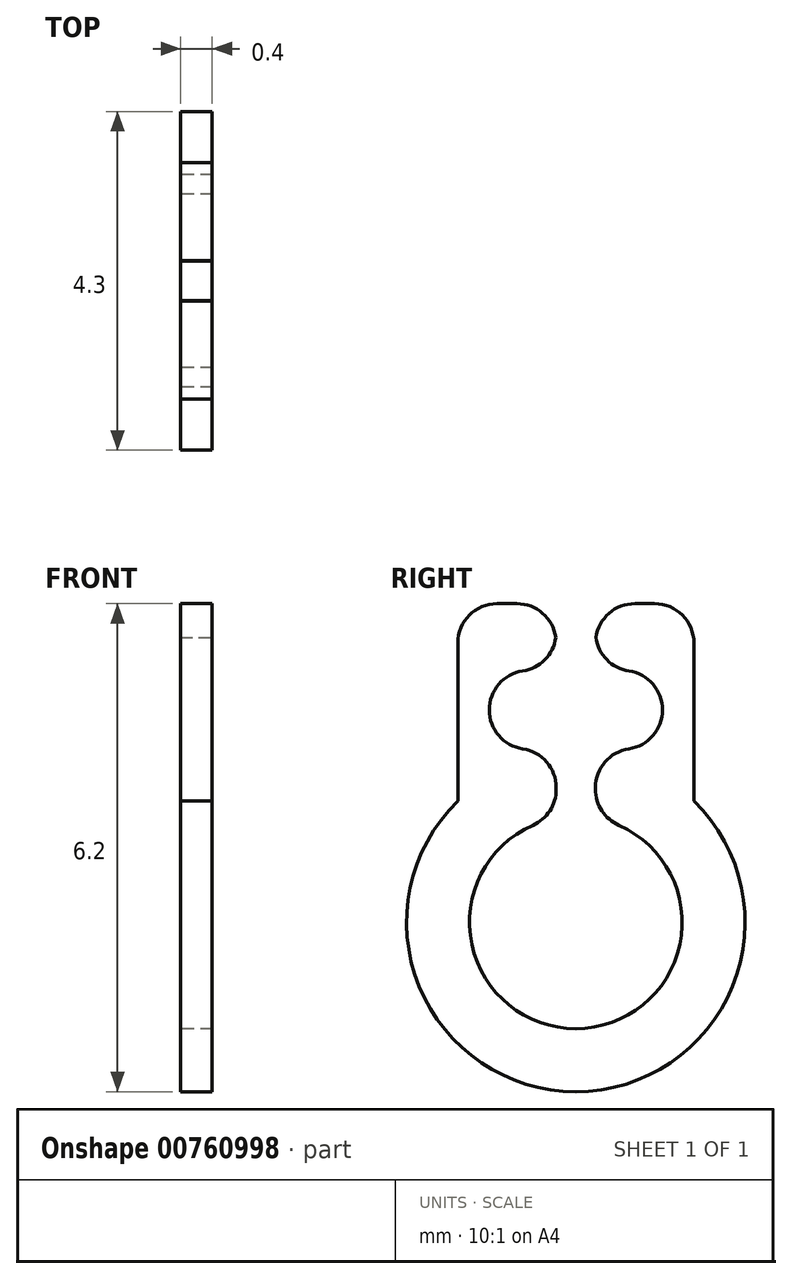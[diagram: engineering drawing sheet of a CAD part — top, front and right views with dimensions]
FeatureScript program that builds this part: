
annotation { "Feature Type Name" : "Feature", "Feature Type Description" : "" }
export const myFeature = defineFeature(function(context is Context, id is Id, definition is map)
    precondition{}
    {
        {
            var Q0;
            Q0=qCreatedBy(makeId("Right.planeOp"),FACE);
            var sketch = newSketch(context, id + "F0", { "sketchPlane" : qUnion([Q0])});
            skArc(sketch, "E0", {"start": v(-0.25, 1.33) * mm, "mid": v(0, -1.35) * mm, "end": v(0.25, 1.33) * mm});
            skArc(sketch, "E1", {"start": v(-1.5, 1.54) * mm, "mid": v(0, -2.15) * mm, "end": v(1.5, 1.54) * mm});
            skPoint(sketch, "E2.center.orphan", {"position": v(-0.7, 2.7) * mm});
            skPoint(sketch, "E3.center.orphan", {"position": v(0.7, 2.7) * mm});
            skLineSegment(sketch, "E4", {"start": v(-1.5, 1.54) * mm, "end": v(-1.5, 4.05) * mm});
            skLineSegment(sketch, "E5", {"start": v(-1.5, 4.05) * mm, "end": v(-0.25, 4.05) * mm});
            skLineSegment(sketch, "E6", {"start": v(1.5, 4.05) * mm, "end": v(1.5, 1.54) * mm});
            skLineSegment(sketch, "E7", {"start": v(-0.6, 2.7) * mm, "end": v(0.6, 2.7) * mm});
            skArc(sketch, "E8.0.startCap", {"start": v(-0.6, 2.2) * mm, "mid": v(-1.1, 2.7) * mm, "end": v(-0.6, 3.2) * mm});
            skArc(sketch, "E8.0.endCap", {"start": v(0.6, 3.2) * mm, "mid": v(1.1, 2.7) * mm, "end": v(0.6, 2.2) * mm});
            skLineSegment(sketch, "E8.0.left", {"start": v(-0.6, 3.2) * mm, "end": v(-0.25, 3.2) * mm});
            skLineSegment(sketch, "E8.0.right", {"start": v(-0.6, 2.2) * mm, "end": v(-0.25, 2.2) * mm});
            skLineSegment(sketch, "E9", {"start": v(-0.25, 4.05) * mm, "end": v(-0.25, 3.2) * mm});
            skLineSegment(sketch, "E10", {"start": v(0.25, 4.05) * mm, "end": v(0.25, 3.2) * mm});
            skLineSegment(sketch, "E11.trimOffspring", {"start": v(0.25, 4.05) * mm, "end": v(1.5, 4.05) * mm});
            skLineSegment(sketch, "E12.trimOffspring", {"start": v(0.25, 3.2) * mm, "end": v(0.6, 3.2) * mm});
            skLineSegment(sketch, "E13.trimOffspring", {"start": v(-0.25, 2.2) * mm, "end": v(-0.25, 1.33) * mm});
            skLineSegment(sketch, "E14.trimOffspring", {"start": v(0.25, 2.2) * mm, "end": v(0.25, 1.33) * mm});
            skLineSegment(sketch, "E15.trimOffspring", {"start": v(0.25, 2.2) * mm, "end": v(0.6, 2.2) * mm});
            skSolve(sketch);
        }
        {
            var Q0;
            Q0 = qSketchRegion(id + "F0", true);
            extrude(context, id + "F1", {"entities" : qUnion([Q0]), "depth" : 0.4 * mm, "offsetDistance" : 25 * mm});
        }
        {
            var Q0;
            Q0=makeQuery(id+"F1.opExtrude","SWEPT_EDGE",EDGE,{"disambiguationData":[OSD([sQuery(id+"F0.wireOp",EDGE,"E5"),sQuery(id+"F0.wireOp",EDGE,"E9")])]});
            var Q1;
            Q1=makeQuery(id+"F1.opExtrude","SWEPT_EDGE",EDGE,{"disambiguationData":[OSD([sQuery(id+"F0.wireOp",EDGE,"E8.0.left"),sQuery(id+"F0.wireOp",EDGE,"E9")])]});
            var Q2;
            Q2=makeQuery(id+"F1.opExtrude","SWEPT_EDGE",EDGE,{"disambiguationData":[OSD([sQuery(id+"F0.wireOp",EDGE,"E4"),sQuery(id+"F0.wireOp",EDGE,"E5")])]});
            var Q3;
            Q3=makeQuery(id+"F1.opExtrude","SWEPT_EDGE",EDGE,{"disambiguationData":[OSD([sQuery(id+"F0.wireOp",EDGE,"E8.0.right"),sQuery(id+"F0.wireOp",EDGE,"E13.trimOffspring")])]});
            var Q4;
            Q4=makeQuery(id+"F1.opExtrude","SWEPT_EDGE",EDGE,{"disambiguationData":[OSD([sQuery(id+"F0.wireOp",EDGE,"E14.trimOffspring"),sQuery(id+"F0.wireOp",EDGE,"E15.trimOffspring")])]});
            var Q5;
            Q5=makeQuery(id+"F1.opExtrude","SWEPT_EDGE",EDGE,{"disambiguationData":[OSD([sQuery(id+"F0.wireOp",EDGE,"E10"),sQuery(id+"F0.wireOp",EDGE,"E11.trimOffspring")])]});
            var Q6;
            Q6=makeQuery(id+"F1.opExtrude","SWEPT_EDGE",EDGE,{"disambiguationData":[OSD([sQuery(id+"F0.wireOp",EDGE,"E10"),sQuery(id+"F0.wireOp",EDGE,"E12.trimOffspring")])]});
            var Q7;
            Q7=makeQuery(id+"F1.opExtrude","SWEPT_EDGE",EDGE,{"disambiguationData":[OSD([sQuery(id+"F0.wireOp",EDGE,"E6"),sQuery(id+"F0.wireOp",EDGE,"E11.trimOffspring")])]});
            var Q8;
            Q8=makeQuery(id+"F1.opExtrude","SWEPT_EDGE",EDGE,{"disambiguationData":[OSD([sQuery(id+"F0.wireOp",EDGE,"E0"),sQuery(id+"F0.wireOp",EDGE,"E14.trimOffspring")])]});
            var Q9;
            Q9=makeQuery(id+"F1.opExtrude","SWEPT_EDGE",EDGE,{"disambiguationData":[OSD([sQuery(id+"F0.wireOp",EDGE,"E0"),sQuery(id+"F0.wireOp",EDGE,"E13.trimOffspring")])]});
            fillet(context, id + "F2", {"entities" : qUnion([Q0, Q1, Q2, Q3, Q4, Q5, Q6, Q7, Q8, Q9]), "radius" : 0.5 * mm, "tangentPropagation" : true, "allowEdgeOverflow" : false});
        }
    });
